# Revit family: Legrand-Industrial_Enclosures-Metal-Altis_Cabinets-D_500
name_source: partatom
category: Equipement électrique
units: mm (PartAtom-declared; Revit-internal decimal feet)

## family parameters
Basée sur le plan de construction = Non
Configuration du panneau = Deux colonnes, circuits au sein
Cote de connecteur circulaire = Utiliser le diamètre
Couper avec des vides une fois chargée = Non
Numéro OmniClass = 23.80.30.11.17
Partagée = Non
Point de calcul de pièce = Non
Titre OmniClass = Distribution Boards and Control Panels
Toujours verticalement = Oui
Type d'élément = Tableau de raccordement

## types (15) — shared parameters
ETIM Class 6.0 = EC000261
Fabricant = Legrand
General Conditions of Use = https://export.legrand.com
IK = 10
IP = 55
Material = Polyester
RAL = 7035
URL = www.legrand.fr
depth = 500 mm  [stored 1.64042 ft]
error double plinth height = Non
no plinth = Oui
plinth height 100 width 1000 = Non
plinth height 100 width 1200 = Non
plinth height 100 width 1600 = Non
plinth height 100 width 400 = Non
plinth height 100 width 600 = Non
plinth height 100 width 800 = Non
plinth height 200 width 1000 = Non
plinth height 200 width 1200 = Non
plinth height 200 width 1600 = Non
plinth height 200 width 400 = Non
plinth height 200 width 600 = Non
plinth height 200 width 800 = Non
socle 100mm = Non
socle 200mm = Non
zero-valued in all types: Elévation par défaut, plinth height

## per-type parameters (varying)
| type | Cabinet 047220 | Cabinet 047221 | Cabinet 047222 | Cabinet 047223 | Cabinet 047224 | Cabinet 047225 | Cabinet 047226 | Cabinet 047227 | Cabinet 047228 | Cabinet 047229 | Cabinet 047230 | Cabinet 047231 | Cabinet 047232 | Cabinet 047233 | Cabinet 047234 | Depth installation zone | Description | Image du type | Width installation zone | distance to installation zone | height | weight | width |
| Industrial enclosures - Altis - Assemblable - Metal - Depth 500mm - Height 1600mm - Width  600mm | Oui | Non | Non | Non | Non | Non | Non | Non | Non | Non | Non | Non | Non | Non | Non | 1100 mm | Ref 047220 - Enveloppe industrielle - Altis - Assemblable - Métal - Profondeur 500mm | Altis_047101_pw_133028_pz_48.jpg | 2200 mm | 600 mm | 1623 mm  [stored 5.3248 ft] | 70.40 kg | 600 mm |
| Industrial enclosures - Altis - Assemblable - Metal - Depth 500mm - Height 1600mm - Width  800mm | Non | Oui | Non | Non | Non | Non | Non | Non | Non | Non | Non | Non | Non | Non | Non | 1300 mm  [stored 4.26509 ft] | Ref 047221 - Enveloppe industrielle - Altis - Assemblable - Métal - Profondeur 500mm | Altis_047101_pw_133028_pz_48.jpg | 2400 mm | 800 mm  [stored 2.62467 ft] | 1623 mm  [stored 5.3248 ft] | 81.00 kg | 800 mm  [stored 2.62467 ft] |
| Industrial enclosures - Altis - Assemblable - Metal - Depth 500mm - Height 1600mm - Width  1200mm | Non | Non | Oui | Non | Non | Non | Non | Non | Non | Non | Non | Non | Non | Non | Non | 500 mm  [stored 1.64042 ft] | Ref 047222 - Enveloppe industrielle - Altis - Assemblable - Métal - Profondeur 500mm | Altis_047101_pw_133028_pz_48.jpg | 1600 mm  [stored 5.24934 ft] | 0 mm  [stored 0 ft] | 1623 mm  [stored 5.3248 ft] | 124.50 kg | 0 mm  [stored 0 ft] |
| Industrial enclosures - Altis - Assemblable - Metal - Depth 500mm - Height 1800mm - Width  400mm | Non | Non | Non | Oui | Non | Non | Non | Non | Non | Non | Non | Non | Non | Non | Non | 900 mm  [stored 2.95276 ft] | Ref 047223 - Enveloppe industrielle - Altis - Assemblable - Métal - Profondeur 500mm | Altis_047101_pw_133028_pz_48.jpg | 2000 mm  [stored 6.56168 ft] | 400 mm  [stored 1.31234 ft] | 1823 mm  [stored 5.98097 ft] | 55.00 kg | 400 mm  [stored 1.31234 ft] |
| Industrial enclosures - Altis - Assemblable - Metal - Depth 500mm - Height 1800mm - Width  600mm | Non | Non | Non | Non | Oui | Non | Non | Non | Non | Non | Non | Non | Non | Non | Non | 1100 mm | Ref 047224 - Enveloppe industrielle - Altis - Assemblable - Métal - Profondeur 500mm | Altis_047101_pw_133028_pz_48.jpg | 2200 mm | 600 mm | 1823 mm  [stored 5.98097 ft] | 74.30 kg | 600 mm |
| Industrial enclosures - Altis - Assemblable - Metal - Depth 500mm - Height 1800mm - Width  800mm | Non | Non | Non | Non | Non | Oui | Non | Non | Non | Non | Non | Non | Non | Non | Non | 1300 mm  [stored 4.26509 ft] | Ref 047225 - Enveloppe industrielle - Altis - Assemblable - Métal - Profondeur 500mm | Altis_047101_pw_133028_pz_48.jpg | 2400 mm | 800 mm  [stored 2.62467 ft] | 1823 mm  [stored 5.98097 ft] | 86.00 kg | 800 mm  [stored 2.62467 ft] |
| Industrial enclosures - Altis - Assemblable - Metal - Depth 500mm - Height 1800mm - Width 1000mm - With door recentring | Non | Non | Non | Non | Non | Non | Oui | Non | Non | Non | Non | Non | Non | Non | Non | 1500 mm  [stored 4.92126 ft] | Ref 047226 - Enveloppe industrielle - Altis - Assemblable - Métal - Profondeur 500mm | <Aucun> | 2600 mm  [stored 8.53018 ft] | 1000 mm  [stored 3.28084 ft] | 1823 mm  [stored 5.98097 ft] | 99.30 kg | 1000 mm  [stored 3.28084 ft] |
| Industrial enclosures - Altis - Assemblable - Metal - Depth 500mm - Height 1800mm - Width  1200mm | Non | Non | Non | Non | Non | Non | Non | Oui | Non | Non | Non | Non | Non | Non | Non | 1700 mm  [stored 5.57743 ft] | Ref 047227 - Enveloppe industrielle - Altis - Assemblable - Métal - Profondeur 500mm | Altis_047101_pw_133028_pz_48.jpg | 2800 mm  [stored 9.18635 ft] | 1200 mm | 1823 mm  [stored 5.98097 ft] | 131.40 kg | 1200 mm |
| Industrial enclosures - Altis - Assemblable - Metal - Depth 500mm - Height 2000mm - Width  400mm | Non | Non | Non | Non | Non | Non | Non | Non | Oui | Non | Non | Non | Non | Non | Non | 900 mm  [stored 2.95276 ft] | Ref 047228 - Enveloppe industrielle - Altis - Assemblable - Métal - Profondeur 500mm | Altis_047101_pw_133028_pz_48.jpg | 2000 mm  [stored 6.56168 ft] | 400 mm  [stored 1.31234 ft] | 2023 mm  [stored 6.63714 ft] | 57.50 kg | 400 mm  [stored 1.31234 ft] |
| Industrial enclosures - Altis - Assemblable - Metal - Depth 500mm - Height 2000mm - Width  600mm | Non | Non | Non | Non | Non | Non | Non | Non | Non | Oui | Non | Non | Non | Non | Non | 1100 mm | Ref 047229 - Enveloppe industrielle - Altis - Assemblable - Métal - Profondeur 500mm | Altis_047101_pw_133028_pz_48.jpg | 2200 mm | 600 mm | 2023 mm  [stored 6.63714 ft] | 79.20 kg | 600 mm |
| Industrial enclosures - Altis - Assemblable - Metal - Depth 500mm - Height 2000mm - Width  800mm | Non | Non | Non | Non | Non | Non | Non | Non | Non | Non | Oui | Non | Non | Non | Non | 1300 mm  [stored 4.26509 ft] | Ref 047230 - Enveloppe industrielle - Altis - Assemblable - Métal - Profondeur 500mm | Altis_047101_pw_133028_pz_48.jpg | 2400 mm | 800 mm  [stored 2.62467 ft] | 2023 mm  [stored 6.63714 ft] | 92.70 kg | 800 mm  [stored 2.62467 ft] |
| Industrial enclosures - Altis - Assemblable - Metal - Depth 500mm - Height 2000mm - Width 1000mm - With door recentring | Non | Non | Non | Non | Non | Non | Non | Non | Non | Non | Non | Oui | Non | Non | Non | 1500 mm  [stored 4.92126 ft] | Ref 047231 - Enveloppe industrielle - Altis - Assemblable - Métal - Profondeur 500mm | <Aucun> | 2600 mm  [stored 8.53018 ft] | 1000 mm  [stored 3.28084 ft] | 2023 mm  [stored 6.63714 ft] | 106.00 kg | 1000 mm  [stored 3.28084 ft] |
| Industrial enclosures - Altis - Assemblable - Metal - Depth 500mm - Height 2000mm - Width  1000mm | Non | Non | Non | Non | Non | Non | Non | Non | Non | Non | Non | Non | Oui | Non | Non | 1500 mm  [stored 4.92126 ft] | Ref 047232 - Enveloppe industrielle - Altis - Assemblable - Métal - Profondeur 500mm | Altis_047101_pw_133028_pz_48.jpg | 2600 mm  [stored 8.53018 ft] | 1000 mm  [stored 3.28084 ft] | 2023 mm  [stored 6.63714 ft] | 110.70 kg | 1000 mm  [stored 3.28084 ft] |
| Industrial enclosures - Altis - Assemblable - Metal - Depth 500mm - Height 2000mm - Width 1200mm | Non | Non | Non | Non | Non | Non | Non | Non | Non | Non | Non | Non | Non | Oui | Non | 1700 mm  [stored 5.57743 ft] | Ref 047233 - Enveloppe industrielle - Altis - Assemblable - Métal - Profondeur 500mm | Altis_047101_pw_133028_pz_48.jpg | 2800 mm  [stored 9.18635 ft] | 1200 mm | 2023 mm  [stored 6.63714 ft] | 138.00 kg | 1200 mm |
| Industrial enclosures - Altis - Assemblable - Metal - Depth 500mm - Height 2000mm - Width 1600mm | Non | Non | Non | Non | Non | Non | Non | Non | Non | Non | Non | Non | Non | Non | Oui | 2100 mm | Ref 047234 - Enveloppe industrielle - Altis - Assemblable - Métal - Profondeur 500mm | Altis_047101_pw_133028_pz_48.jpg | 3200 mm  [stored 10.4987 ft] | 1600 mm  [stored 5.24934 ft] | 2023 mm  [stored 6.63714 ft] | 147.00 kg | 1600 mm  [stored 5.24934 ft] |

note: [stored X ft] marks values corroborated as IEEE doubles in the binary element streams (Revit-internal decimal feet)
